# Revit family: AD-S.SAT - X Mount
name_source: partatom
category: Generic Models
revit_build: Autodesk Revit 2015 (Build: 20160512_0715(x64)
units: mm (PartAtom-declared; Revit-internal decimal feet)

## types (1)
- AD-S.SAT - X Mount
    Coverage Horizontal = 170.00°
    Coverage Vertical = 170.00°
    Default Elevation = 4' - 0"
    Depth = 0' - 5 13/32"
    Description = 2.75-inch Small Format Surface Satellite Loudspeaker
    Height = 0' - 3 19/32"
    Manufacturer = QSC
    Manufacturer URL = www.qsc.com
    Model = AD-S.SAT
    Mount Depth = 0' - 0 31/32"
    Mount Height = 0' - 5 9/32"
    Mount Width = 0' - 4 11/32"
    Product Documentation Link = https://www.qsc.com
    Product Page URL = https://www.qsc.com
    Regulatory Compliance = Transformer UL registered per UL1876, ROHS, CE compliant
    SPL Max = 90
    Sensitivity = 82
    Weight Product (kg) = 0.433
    Weight Product (lb) = 0.95
    Width = 0' - 3 1/2"

## geometry (parser evidence)
native form markers: Blend x8, Sweep x16
no freeform markers — native parametric forms only
